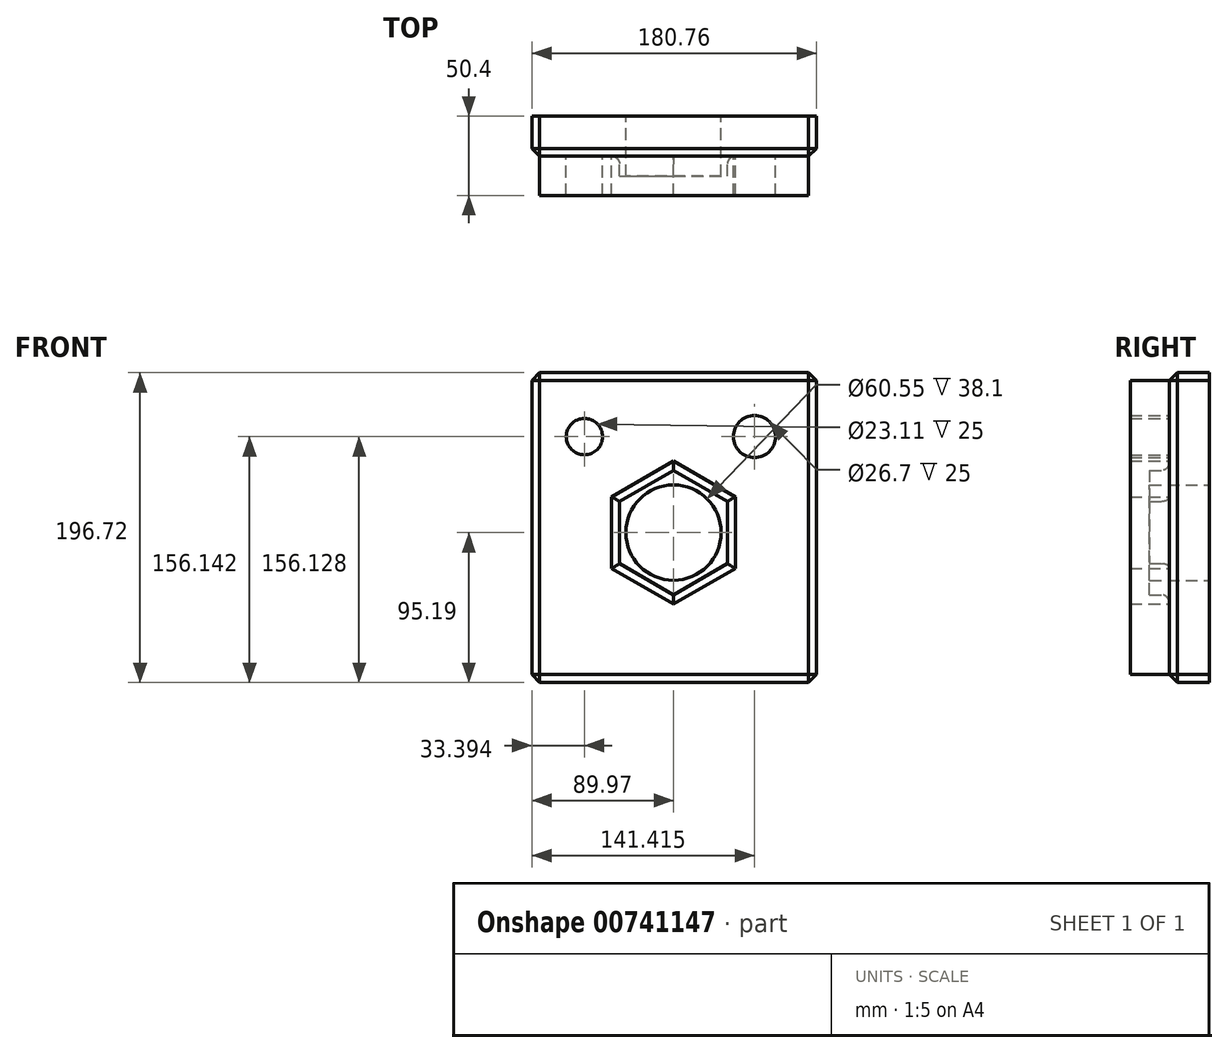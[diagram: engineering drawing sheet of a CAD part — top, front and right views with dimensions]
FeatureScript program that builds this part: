
annotation { "Feature Type Name" : "Feature", "Feature Type Description" : "" }
export const myFeature = defineFeature(function(context is Context, id is Id, definition is map)
    precondition{}
    {
        {
            var Q0;
            Q0=qCreatedBy(makeId("Front.planeOp"),FACE);
            var sketch = newSketch(context, id + "F0", { "sketchPlane" : qUnion([Q0])});
            skCircle(sketch, "E0.cCircle", {"center": v(0, 0) * mm, "radius": 34.25 * mm, "construction": true});
            skLineSegment(sketch, "E0.0", {"start": v(34.25, 19.78) * mm, "end": v(34.25, -19.78) * mm});
            skLineSegment(sketch, "E0.1", {"start": v(34.25, -19.78) * mm, "end": v(0, -39.55) * mm});
            skLineSegment(sketch, "E0.2", {"start": v(0, -39.55) * mm, "end": v(-34.25, -19.78) * mm});
            skLineSegment(sketch, "E0.3", {"start": v(-34.25, -19.78) * mm, "end": v(-34.25, 19.78) * mm});
            skLineSegment(sketch, "E0.4", {"start": v(-34.25, 19.78) * mm, "end": v(0, 39.55) * mm});
            skLineSegment(sketch, "E0.5", {"start": v(0, 39.55) * mm, "end": v(34.25, 19.78) * mm});
            skPoint(sketch, "E0.0.midPoint", {"position": v(34.25, 0) * mm});
            skSolve(sketch);
        }
        {
            var Q0;
            Q0=makeQuery(id+"F0.imprint","IMPRINT",FACE,{"disambiguationData":[TD([[makeQuery(id+"F0.imprint","IMPRINT",EDGE,{"derivedFrom":sQuery(id+"F0.wireOp",EDGE,"E0.0")}),-1.0]])]});
            extrude(context, id + "F1", {"entities" : qUnion([Q0]), "depth" : 38.1 * mm, "offsetDistance" : 25.4 * mm});
        }
        {
            var Q0;
            Q0=makeQuery(id+"F1.opExtrude","CAP_FACE",FACE,{"disambiguationData":[OSD([sQuery(id+"F0.wireOp",EDGE,"E0.0"),sQuery(id+"F0.wireOp",EDGE,"E0.1"),sQuery(id+"F0.wireOp",EDGE,"E0.2"),sQuery(id+"F0.wireOp",EDGE,"E0.3"),sQuery(id+"F0.wireOp",EDGE,"E0.4"),sQuery(id+"F0.wireOp",EDGE,"E0.5")])],"isStart":true});
            var sketch = newSketch(context, id + "F3", { "sketchPlane" : qUnion([Q0])});
            skCircle(sketch, "E1", {"center": v(0, 0) * mm, "radius": 30.27 * mm});
            skSolve(sketch);
        }
        {
            var Q0;
            Q0=makeQuery(id+"F3.imprint","IMPRINT",FACE,{"disambiguationData":[TD([[makeQuery(id+"F3.imprint","IMPRINT",EDGE,{"derivedFrom":sQuery(id+"F3.wireOp",EDGE,"E1")}),1.0]])]});
            extrude(context, id + "F4", {"entities" : qUnion([Q0]), "operationType" : NewBodyOperationType.REMOVE, "oppositeDirection" : true, "depth" : 94.74 * mm, "offsetDistance" : 25.4 * mm});
        }
        {
            var Q0;
            Q0=qCreatedBy(makeId("Front.planeOp"),FACE);
            var sketch = newSketch(context, id + "F5", { "sketchPlane" : qUnion([Q0])});
            skLineSegment(sketch, "E2.bottom", {"start": v(-89.97, 101.53) * mm, "end": v(90.8, 101.53) * mm});
            skLineSegment(sketch, "E2.top", {"start": v(-89.97, -95.19) * mm, "end": v(90.8, -95.19) * mm});
            skLineSegment(sketch, "E2.left", {"start": v(-89.97, 101.53) * mm, "end": v(-89.97, -95.19) * mm});
            skLineSegment(sketch, "E2.right", {"start": v(90.8, 101.53) * mm, "end": v(90.8, -95.19) * mm});
            skSolve(sketch);
        }
        {
            var Q0;
            Q0=makeQuery(id+"F5.imprint","IMPRINT",FACE,{"disambiguationData":[TD([[makeQuery(id+"F5.imprint","IMPRINT",EDGE,{"derivedFrom":sQuery(id+"F5.wireOp",EDGE,"E2.bottom")}),-1.0]])]});
            extrude(context, id + "F6", {"entities" : qUnion([Q0]), "operationType" : NewBodyOperationType.ADD, "depth" : 25.4 * mm, "offsetDistance" : 25.4 * mm});
        }
        {
            var Q0;
            Q0=makeQuery(id+"F6.boolean.opBoolean","SPLIT",FACE,{"disambiguationData":[TD([makeQuery(id+"F4.boolean.opBoolean","COPY",FACE,{"derivedFrom":makeQuery(id+"F4.opExtrude","SWEPT_FACE",FACE,{"disambiguationData":[OSD([sQuery(id+"F3.wireOp",EDGE,"E1")])]})})])],"derivedFrom":makeQuery(id+"F6.opExtrude","CAP_FACE",FACE,{"disambiguationData":[OSD([sQuery(id+"F5.wireOp",EDGE,"E2.bottom"),sQuery(id+"F5.wireOp",EDGE,"E2.top"),sQuery(id+"F5.wireOp",EDGE,"E2.left"),sQuery(id+"F5.wireOp",EDGE,"E2.right")])],"isStart":false})});
            extrude(context, id + "F7", {"entities" : qUnion([Q0]), "operationType" : NewBodyOperationType.REMOVE, "oppositeDirection" : true, "depth" : 107.11 * mm, "offsetDistance" : 25 * mm});
        }
        {
            var Q0;
            Q0=makeQuery(id+"F6.boolean.opBoolean","INTERSECT",EDGE,{"derivedFrom":[makeQuery(id+"F1.opExtrude","SWEPT_FACE",FACE,{"disambiguationData":[OSD([sQuery(id+"F0.wireOp",EDGE,"E0.5")])]}),makeQuery(id+"F6.opExtrude","CAP_FACE",FACE,{"disambiguationData":[OSD([sQuery(id+"F5.wireOp",EDGE,"E2.bottom"),sQuery(id+"F5.wireOp",EDGE,"E2.top"),sQuery(id+"F5.wireOp",EDGE,"E2.left"),sQuery(id+"F5.wireOp",EDGE,"E2.right")])],"isStart":false})]});
            var Q1;
            Q1=makeQuery(id+"F6.boolean.opBoolean","INTERSECT",EDGE,{"derivedFrom":[makeQuery(id+"F1.opExtrude","SWEPT_FACE",FACE,{"disambiguationData":[OSD([sQuery(id+"F0.wireOp",EDGE,"E0.4")])]}),makeQuery(id+"F6.opExtrude","CAP_FACE",FACE,{"disambiguationData":[OSD([sQuery(id+"F5.wireOp",EDGE,"E2.bottom"),sQuery(id+"F5.wireOp",EDGE,"E2.top"),sQuery(id+"F5.wireOp",EDGE,"E2.left"),sQuery(id+"F5.wireOp",EDGE,"E2.right")])],"isStart":false})]});
            var Q2;
            Q2=makeQuery(id+"F6.boolean.opBoolean","INTERSECT",EDGE,{"derivedFrom":[makeQuery(id+"F1.opExtrude","SWEPT_FACE",FACE,{"disambiguationData":[OSD([sQuery(id+"F0.wireOp",EDGE,"E0.0")])]}),makeQuery(id+"F6.opExtrude","CAP_FACE",FACE,{"disambiguationData":[OSD([sQuery(id+"F5.wireOp",EDGE,"E2.bottom"),sQuery(id+"F5.wireOp",EDGE,"E2.top"),sQuery(id+"F5.wireOp",EDGE,"E2.left"),sQuery(id+"F5.wireOp",EDGE,"E2.right")])],"isStart":false})]});
            var Q3;
            Q3=makeQuery(id+"F6.boolean.opBoolean","INTERSECT",EDGE,{"derivedFrom":[makeQuery(id+"F1.opExtrude","SWEPT_FACE",FACE,{"disambiguationData":[OSD([sQuery(id+"F0.wireOp",EDGE,"E0.1")])]}),makeQuery(id+"F6.opExtrude","CAP_FACE",FACE,{"disambiguationData":[OSD([sQuery(id+"F5.wireOp",EDGE,"E2.bottom"),sQuery(id+"F5.wireOp",EDGE,"E2.top"),sQuery(id+"F5.wireOp",EDGE,"E2.left"),sQuery(id+"F5.wireOp",EDGE,"E2.right")])],"isStart":false})]});
            var Q4;
            Q4=makeQuery(id+"F6.boolean.opBoolean","INTERSECT",EDGE,{"derivedFrom":[makeQuery(id+"F1.opExtrude","SWEPT_FACE",FACE,{"disambiguationData":[OSD([sQuery(id+"F0.wireOp",EDGE,"E0.2")])]}),makeQuery(id+"F6.opExtrude","CAP_FACE",FACE,{"disambiguationData":[OSD([sQuery(id+"F5.wireOp",EDGE,"E2.bottom"),sQuery(id+"F5.wireOp",EDGE,"E2.top"),sQuery(id+"F5.wireOp",EDGE,"E2.left"),sQuery(id+"F5.wireOp",EDGE,"E2.right")])],"isStart":false})]});
            var Q5;
            Q5=makeQuery(id+"F6.boolean.opBoolean","INTERSECT",EDGE,{"derivedFrom":[makeQuery(id+"F1.opExtrude","SWEPT_FACE",FACE,{"disambiguationData":[OSD([sQuery(id+"F0.wireOp",EDGE,"E0.3")])]}),makeQuery(id+"F6.opExtrude","CAP_FACE",FACE,{"disambiguationData":[OSD([sQuery(id+"F5.wireOp",EDGE,"E2.bottom"),sQuery(id+"F5.wireOp",EDGE,"E2.top"),sQuery(id+"F5.wireOp",EDGE,"E2.left"),sQuery(id+"F5.wireOp",EDGE,"E2.right")])],"isStart":false})]});
            fillet(context, id + "F8", {"entities" : qUnion([Q0, Q1, Q2, Q3, Q4, Q5]), "radius" : 5 * mm, "tangentPropagation" : true, "allowEdgeOverflow" : false});
        }
        {
            var Q0;
            Q0=makeQuery(id+"F6.opExtrude","SWEPT_EDGE",EDGE,{"disambiguationData":[OSD([sQuery(id+"F5.wireOp",EDGE,"E2.bottom"),sQuery(id+"F5.wireOp",EDGE,"E2.right")])]});
            var Q1;
            {var subQ0=sQuery(id+"F5.wireOp",EDGE,"E2.bottom");var subQ1=sQuery(id+"F5.wireOp",EDGE,"E2.top");var subQ2=sQuery(id+"F5.wireOp",EDGE,"E2.left");var subQ3=sQuery(id+"F5.wireOp",EDGE,"E2.right");Q1=makeQuery(id+"F6.boolean.opBoolean","SPLIT",FACE,{"disambiguationData":[TD([makeQuery(id+"F1.opExtrude","SWEPT_FACE",FACE,{"disambiguationData":[OSD([sQuery(id+"F0.wireOp",EDGE,"E0.0")])]})])],"derivedFrom":makeQuery(id+"F6.opExtrude","CAP_FACE",FACE,{"disambiguationData":[OSD([subQ0,subQ1,subQ2,subQ3])],"isStart":false})});}
            var Q2;
            Q2=makeQuery(id+"F6.opExtrude","SWEPT_EDGE",EDGE,{"disambiguationData":[OSD([sQuery(id+"F5.wireOp",EDGE,"E2.bottom"),sQuery(id+"F5.wireOp",EDGE,"E2.left")])]});
            var Q3;
            Q3=makeQuery(id+"F6.opExtrude","SWEPT_EDGE",EDGE,{"disambiguationData":[OSD([sQuery(id+"F5.wireOp",EDGE,"E2.top"),sQuery(id+"F5.wireOp",EDGE,"E2.left")])]});
            var Q4;
            Q4=makeQuery(id+"F6.opExtrude","SWEPT_EDGE",EDGE,{"disambiguationData":[OSD([sQuery(id+"F5.wireOp",EDGE,"E2.top"),sQuery(id+"F5.wireOp",EDGE,"E2.right")])]});
            chamfer(context, id + "F9", {"entities" : qUnion([Q0, Q1, Q2, Q3, Q4]), "width" : 5 * mm, "tangentPropagation" : true});
        }
        {
            var Q0;
            {var subQ0=sQuery(id+"F5.wireOp",EDGE,"E2.bottom");var subQ1=sQuery(id+"F5.wireOp",EDGE,"E2.top");var subQ2=sQuery(id+"F5.wireOp",EDGE,"E2.left");var subQ3=sQuery(id+"F5.wireOp",EDGE,"E2.right");Q0=makeQuery(id+"F6.boolean.opBoolean","SPLIT",FACE,{"disambiguationData":[TD([makeQuery(id+"F1.opExtrude","SWEPT_FACE",FACE,{"disambiguationData":[OSD([sQuery(id+"F0.wireOp",EDGE,"E0.0")])]})])],"derivedFrom":makeQuery(id+"F6.opExtrude","CAP_FACE",FACE,{"disambiguationData":[OSD([subQ0,subQ1,subQ2,subQ3])],"isStart":false})});}
            var sketch = newSketch(context, id + "F10", { "sketchPlane" : qUnion([Q0])});
            skCircle(sketch, "E3", {"center": v(-56.58, 60.94) * mm, "radius": 11.56 * mm});
            skSolve(sketch);
        }
        {
            var Q0;
            Q0=makeQuery(id+"F10.imprint","IMPRINT",FACE,{"disambiguationData":[TD([[makeQuery(id+"F10.imprint","IMPRINT",EDGE,{"derivedFrom":sQuery(id+"F10.wireOp",EDGE,"E3")}),-1.0]])]});
            var sketch = newSketch(context, id + "F11", { "sketchPlane" : qUnion([Q0])});
            skCircle(sketch, "E4", {"center": v(51.44, 60.95) * mm, "radius": 13.35 * mm});
            skSolve(sketch);
        }
        {
            var Q0;
            Q0=makeQuery(id+"F11.imprint","IMPRINT",FACE,{"disambiguationData":[TD([[makeQuery(id+"F11.imprint","IMPRINT",EDGE,{"derivedFrom":sQuery(id+"F11.wireOp",EDGE,"E4")}),-1.0]])]});
            extrude(context, id + "F12", {"entities" : qUnion([Q0]), "operationType" : NewBodyOperationType.ADD, "depth" : 25 * mm, "offsetDistance" : 25 * mm});
        }
    });
